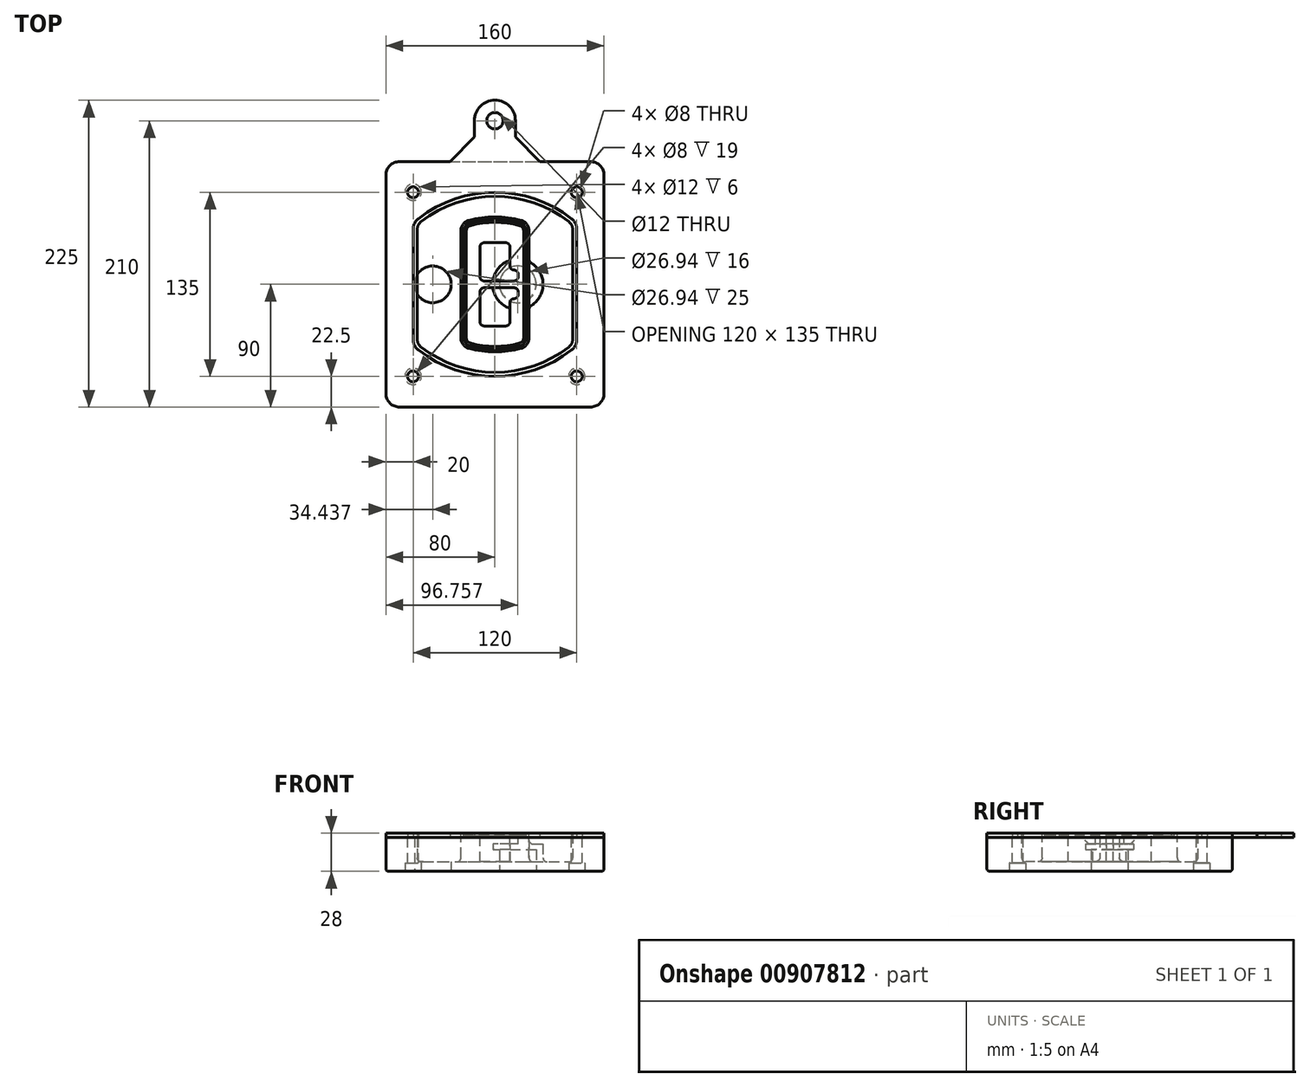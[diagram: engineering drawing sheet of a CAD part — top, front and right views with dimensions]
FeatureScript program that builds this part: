
annotation { "Feature Type Name" : "Feature", "Feature Type Description" : "" }
export const myFeature = defineFeature(function(context is Context, id is Id, definition is map)
    precondition{}
    {
        {
            var Q0;
            Q0=qCreatedBy(makeId("Top.planeOp"),FACE);
            var sketch = newSketch(context, id + "F0", { "sketchPlane" : qUnion([Q0])});
            skPoint(sketch, "E0.rect.middle", {"position": v(0, 0) * mm});
            skLineSegment(sketch, "E1.bottom", {"start": v(-70, -90) * mm, "end": v(70, -90) * mm});
            skLineSegment(sketch, "E1.top", {"start": v(-70, 90) * mm, "end": v(70, 90) * mm});
            skLineSegment(sketch, "E1.left", {"start": v(-80, -80) * mm, "end": v(-80, 80) * mm});
            skLineSegment(sketch, "E1.right", {"start": v(80, -80) * mm, "end": v(80, 80) * mm});
            skLineSegment(sketch, "E2", {"start": v(-80, 90) * mm, "end": v(80, -90) * mm, "construction": true});
            skLineSegment(sketch, "E3", {"start": v(80, 90) * mm, "end": v(-80, -90) * mm, "construction": true});
            skCircle(sketch, "E4", {"center": v(-60, 67.5) * mm, "radius": 4 * mm});
            skCircle(sketch, "E5", {"center": v(60, 67.5) * mm, "radius": 4 * mm});
            skCircle(sketch, "E6", {"center": v(60, -67.5) * mm, "radius": 4 * mm});
            skCircle(sketch, "E7", {"center": v(-60, -67.5) * mm, "radius": 4 * mm});
            skLineSegment(sketch, "E8", {"start": v(-60, 67.5) * mm, "end": v(60, 67.5) * mm, "construction": true});
            skLineSegment(sketch, "E9", {"start": v(60, 67.5) * mm, "end": v(60, -67.5) * mm, "construction": true});
            skLineSegment(sketch, "E10", {"start": v(60, -67.5) * mm, "end": v(-60, -67.5) * mm, "construction": true});
            skLineSegment(sketch, "E11", {"start": v(-60, -67.5) * mm, "end": v(-60, 67.5) * mm, "construction": true});
            skLineSegment(sketch, "E12", {"start": v(-60, 40.3) * mm, "end": v(-60, -40.3) * mm});
            skLineSegment(sketch, "E13", {"start": v(60, 40.3) * mm, "end": v(60, -40.3) * mm});
            skArc(sketch, "E14", {"start": v(56.15, 48.18) * mm, "mid": v(0, 67.5) * mm, "end": v(-56.15, 48.18) * mm});
            skArc(sketch, "E15", {"start": v(-56.15, -48.18) * mm, "mid": v(0, -67.5) * mm, "end": v(56.15, -48.18) * mm});
            skLineSegment(sketch, "E16", {"start": v(-60, 0) * mm, "end": v(60, 0) * mm, "construction": true});
            skPoint(sketch, "E17.visualSharp", {"position": v(-60, -45) * mm});
            skArc(sketch, "E17.filletArc", {"start": v(-60, -40.3) * mm, "mid": v(-58.99, -44.68) * mm, "end": v(-56.15, -48.18) * mm});
            skPoint(sketch, "E18.visualSharp", {"position": v(-60, 45) * mm});
            skArc(sketch, "E18.filletArc", {"start": v(-56.15, 48.18) * mm, "mid": v(-58.99, 44.68) * mm, "end": v(-60, 40.3) * mm});
            skPoint(sketch, "E19.visualSharp", {"position": v(60, 45) * mm});
            skArc(sketch, "E19.filletArc", {"start": v(60, 40.3) * mm, "mid": v(58.99, 44.68) * mm, "end": v(56.15, 48.18) * mm});
            skPoint(sketch, "E20.visualSharp", {"position": v(60, -45) * mm});
            skArc(sketch, "E20.filletArc", {"start": v(56.15, -48.18) * mm, "mid": v(58.99, -44.68) * mm, "end": v(60, -40.3) * mm});
            skPoint(sketch, "E21.visualSharp", {"position": v(-80, 90) * mm});
            skArc(sketch, "E21.filletArc", {"start": v(-70, 90) * mm, "mid": v(-77.07, 87.07) * mm, "end": v(-80, 80) * mm});
            skPoint(sketch, "E22.visualSharp", {"position": v(80, 90) * mm});
            skArc(sketch, "E22.filletArc", {"start": v(80, 80) * mm, "mid": v(77.07, 87.07) * mm, "end": v(70, 90) * mm});
            skPoint(sketch, "E23.visualSharp", {"position": v(80, -90) * mm});
            skArc(sketch, "E23.filletArc", {"start": v(70, -90) * mm, "mid": v(77.07, -87.07) * mm, "end": v(80, -80) * mm});
            skPoint(sketch, "E24.visualSharp", {"position": v(-80, -90) * mm});
            skArc(sketch, "E24.filletArc", {"start": v(-80, -80) * mm, "mid": v(-77.07, -87.07) * mm, "end": v(-70, -90) * mm});
            skArc(sketch, "E25.0", {"start": v(57, 40.3) * mm, "mid": v(56.3, 43.36) * mm, "end": v(54.3, 45.81) * mm});
            skLineSegment(sketch, "E25.1", {"start": v(57, 40.3) * mm, "end": v(57, -40.3) * mm});
            skArc(sketch, "E25.2", {"start": v(54.3, -45.81) * mm, "mid": v(56.3, -43.36) * mm, "end": v(57, -40.3) * mm});
            skArc(sketch, "E25.3", {"start": v(-54.3, -45.81) * mm, "mid": v(0, -64.5) * mm, "end": v(54.3, -45.81) * mm});
            skArc(sketch, "E25.4", {"start": v(-57, -40.3) * mm, "mid": v(-56.3, -43.36) * mm, "end": v(-54.3, -45.81) * mm});
            skArc(sketch, "E25.5", {"start": v(54.3, 45.81) * mm, "mid": v(0, 64.5) * mm, "end": v(-54.3, 45.81) * mm});
            skLineSegment(sketch, "E25.6", {"start": v(-57, 40.3) * mm, "end": v(-57, -40.3) * mm});
            skArc(sketch, "E25.7", {"start": v(-54.3, 45.81) * mm, "mid": v(-56.3, 43.36) * mm, "end": v(-57, 40.3) * mm});
            skArc(sketch, "E26.0", {"start": v(-58.62, 51.33) * mm, "mid": v(-62.58, 46.43) * mm, "end": v(-64, 40.3) * mm});
            skArc(sketch, "E26.1", {"start": v(58.62, 51.33) * mm, "mid": v(0, 71.5) * mm, "end": v(-58.62, 51.33) * mm});
            skArc(sketch, "E26.2", {"start": v(64, 40.3) * mm, "mid": v(62.58, 46.43) * mm, "end": v(58.62, 51.33) * mm});
            skLineSegment(sketch, "E26.3", {"start": v(64, 40.3) * mm, "end": v(64, -40.3) * mm});
            skArc(sketch, "E26.4", {"start": v(58.62, -51.33) * mm, "mid": v(62.58, -46.43) * mm, "end": v(64, -40.3) * mm});
            skLineSegment(sketch, "E26.5", {"start": v(-64, 40.3) * mm, "end": v(-64, -40.3) * mm});
            skArc(sketch, "E26.6", {"start": v(-58.62, -51.33) * mm, "mid": v(0, -71.5) * mm, "end": v(58.62, -51.33) * mm});
            skArc(sketch, "E26.7", {"start": v(-64, -40.3) * mm, "mid": v(-62.58, -46.43) * mm, "end": v(-58.62, -51.33) * mm});
            skSolve(sketch);
        }
        {
            var Q0;
            Q0=makeQuery(id+"F0.imprint","IMPRINT",FACE,{"disambiguationData":[TD([[makeQuery(id+"F0.imprint","IMPRINT",EDGE,{"derivedFrom":sQuery(id+"F0.wireOp",EDGE,"E1.bottom")}),1.0]])]});
            var Q1;
            Q1=makeQuery(id+"F0.imprint","IMPRINT",FACE,{"disambiguationData":[TD([[makeQuery(id+"F0.imprint","IMPRINT",EDGE,{"derivedFrom":sQuery(id+"F0.wireOp",EDGE,"E12")}),1.0]])]});
            var Q2;
            Q2=makeQuery(id+"F0.imprint","IMPRINT",FACE,{"disambiguationData":[TD([[makeQuery(id+"F0.imprint","IMPRINT",EDGE,{"derivedFrom":sQuery(id+"F0.wireOp",EDGE,"E25.0")}),1.0]])]});
            var Q3;
            Q3=makeQuery(id+"F0.imprint","IMPRINT",FACE,{"disambiguationData":[TD([[makeQuery(id+"F0.imprint","IMPRINT",EDGE,{"derivedFrom":sQuery(id+"F0.wireOp",EDGE,"E12")}),-1.0]])]});
            extrude(context, id + "F1", {"entities" : qUnion([Q0, Q1, Q2, Q3]), "oppositeDirection" : true, "depth" : 25 * mm});
        }
        {
            var Q0;
            Q0=makeQuery(id+"F0.imprint","IMPRINT",FACE,{"disambiguationData":[TD([[makeQuery(id+"F0.imprint","IMPRINT",EDGE,{"derivedFrom":sQuery(id+"F0.wireOp",EDGE,"E12")}),1.0]])]});
            extrude(context, id + "F2", {"entities" : qUnion([Q0]), "operationType" : NewBodyOperationType.ADD, "depth" : 3 * mm});
        }
        {
            var Q0;
            Q0=makeQuery(id+"F0.imprint","IMPRINT",FACE,{"disambiguationData":[TD([[makeQuery(id+"F0.imprint","IMPRINT",EDGE,{"derivedFrom":sQuery(id+"F0.wireOp",EDGE,"E25.0")}),1.0]])]});
            extrude(context, id + "F3", {"entities" : qUnion([Q0]), "operationType" : NewBodyOperationType.REMOVE, "oppositeDirection" : true, "depth" : 18 * mm});
        }
        {
            var Q0;
            Q0=makeQuery(id+"F2.opExtrude","CAP_FACE",FACE,{"disambiguationData":[OSD([sQuery(id+"F0.wireOp",EDGE,"E12"),sQuery(id+"F0.wireOp",EDGE,"E13"),sQuery(id+"F0.wireOp",EDGE,"E14"),sQuery(id+"F0.wireOp",EDGE,"E15"),sQuery(id+"F0.wireOp",EDGE,"E17.filletArc"),sQuery(id+"F0.wireOp",EDGE,"E18.filletArc"),sQuery(id+"F0.wireOp",EDGE,"E19.filletArc"),sQuery(id+"F0.wireOp",EDGE,"E20.filletArc"),sQuery(id+"F0.wireOp",EDGE,"E25.0"),sQuery(id+"F0.wireOp",EDGE,"E25.1"),sQuery(id+"F0.wireOp",EDGE,"E25.2"),sQuery(id+"F0.wireOp",EDGE,"E25.3"),sQuery(id+"F0.wireOp",EDGE,"E25.4"),sQuery(id+"F0.wireOp",EDGE,"E25.5"),sQuery(id+"F0.wireOp",EDGE,"E25.6"),sQuery(id+"F0.wireOp",EDGE,"E25.7")])],"isStart":false});
            var sketch = newSketch(context, id + "F4", { "sketchPlane" : qUnion([Q0])});
            skArc(sketch, "E27.0", {"start": v(-19.08, -46.97) * mm, "mid": v(0, -49.5) * mm, "end": v(19.08, -46.97) * mm});
            skArc(sketch, "E28.0", {"start": v(19.08, 46.97) * mm, "mid": v(0, 49.5) * mm, "end": v(-19.08, 46.97) * mm});
            skLineSegment(sketch, "E29", {"start": v(-25, 39.25) * mm, "end": v(-25, -39.25) * mm});
            skLineSegment(sketch, "E30", {"start": v(25, 39.25) * mm, "end": v(25, -39.25) * mm});
            skLineSegment(sketch, "E31", {"start": v(-25, 45.1) * mm, "end": v(25, 45.1) * mm, "construction": true});
            skLineSegment(sketch, "E32", {"start": v(-25, -45.1) * mm, "end": v(25, -45.1) * mm, "construction": true});
            skPoint(sketch, "E33.visualSharp", {"position": v(-25, 45.1) * mm});
            skArc(sketch, "E33.filletArc", {"start": v(-19.08, 46.97) * mm, "mid": v(-23.35, 44.11) * mm, "end": v(-25, 39.25) * mm});
            skPoint(sketch, "E34.visualSharp", {"position": v(25, 45.1) * mm});
            skArc(sketch, "E34.filletArc", {"start": v(25, 39.25) * mm, "mid": v(23.35, 44.11) * mm, "end": v(19.08, 46.97) * mm});
            skPoint(sketch, "E35.visualSharp", {"position": v(25, -45.1) * mm});
            skArc(sketch, "E35.filletArc", {"start": v(19.08, -46.97) * mm, "mid": v(23.35, -44.11) * mm, "end": v(25, -39.25) * mm});
            skPoint(sketch, "E36.visualSharp", {"position": v(-25, -45.1) * mm});
            skArc(sketch, "E36.filletArc", {"start": v(-25, -39.25) * mm, "mid": v(-23.35, -44.11) * mm, "end": v(-19.08, -46.97) * mm});
            skArc(sketch, "E37.0", {"start": v(54.3, 45.81) * mm, "mid": v(0, 64.5) * mm, "end": v(-54.3, 45.81) * mm});
            skArc(sketch, "E37.1", {"start": v(-54.3, 45.81) * mm, "mid": v(-56.3, 43.36) * mm, "end": v(-57, 40.3) * mm});
            skLineSegment(sketch, "E37.2", {"start": v(-57, 40.3) * mm, "end": v(-57, -40.3) * mm});
            skArc(sketch, "E37.3", {"start": v(-57, -40.3) * mm, "mid": v(-56.3, -43.36) * mm, "end": v(-54.3, -45.81) * mm});
            skArc(sketch, "E37.4", {"start": v(-54.3, -45.81) * mm, "mid": v(0, -64.5) * mm, "end": v(54.3, -45.81) * mm});
            skArc(sketch, "E37.5", {"start": v(54.3, -45.81) * mm, "mid": v(56.3, -43.36) * mm, "end": v(57, -40.3) * mm});
            skLineSegment(sketch, "E37.6", {"start": v(57, 40.3) * mm, "end": v(57, -40.3) * mm});
            skArc(sketch, "E37.7", {"start": v(57, 40.3) * mm, "mid": v(56.3, 43.36) * mm, "end": v(54.3, 45.81) * mm});
            skLineSegment(sketch, "E38.0", {"start": v(23, 39.25) * mm, "end": v(23, -39.25) * mm});
            skArc(sketch, "E38.1", {"start": v(18.56, -45.04) * mm, "mid": v(21.76, -42.9) * mm, "end": v(23, -39.25) * mm});
            skArc(sketch, "E38.2", {"start": v(-18.56, -45.04) * mm, "mid": v(0, -47.5) * mm, "end": v(18.56, -45.04) * mm});
            skArc(sketch, "E38.3", {"start": v(-23, -39.25) * mm, "mid": v(-21.76, -42.9) * mm, "end": v(-18.56, -45.04) * mm});
            skLineSegment(sketch, "E38.4", {"start": v(-23, 39.25) * mm, "end": v(-23, -39.25) * mm});
            skArc(sketch, "E38.5", {"start": v(23, 39.25) * mm, "mid": v(21.76, 42.9) * mm, "end": v(18.56, 45.04) * mm});
            skArc(sketch, "E38.6", {"start": v(-18.56, 45.04) * mm, "mid": v(-21.76, 42.9) * mm, "end": v(-23, 39.25) * mm});
            skArc(sketch, "E38.7", {"start": v(18.56, 45.04) * mm, "mid": v(0, 47.5) * mm, "end": v(-18.56, 45.04) * mm});
            skArc(sketch, "E39.0", {"start": v(21, 39.25) * mm, "mid": v(20.18, 41.68) * mm, "end": v(18.04, 43.1) * mm});
            skLineSegment(sketch, "E39.1", {"start": v(21, 39.25) * mm, "end": v(21, -39.25) * mm});
            skArc(sketch, "E39.2", {"start": v(18.04, -43.1) * mm, "mid": v(20.18, -41.68) * mm, "end": v(21, -39.25) * mm});
            skArc(sketch, "E39.3", {"start": v(-18.04, -43.1) * mm, "mid": v(0, -45.5) * mm, "end": v(18.04, -43.1) * mm});
            skArc(sketch, "E39.4", {"start": v(-21, -39.25) * mm, "mid": v(-20.18, -41.68) * mm, "end": v(-18.04, -43.1) * mm});
            skArc(sketch, "E39.5", {"start": v(18.04, 43.1) * mm, "mid": v(0, 45.5) * mm, "end": v(-18.04, 43.1) * mm});
            skLineSegment(sketch, "E39.6", {"start": v(-21, 39.25) * mm, "end": v(-21, -39.25) * mm});
            skArc(sketch, "E39.7", {"start": v(-18.04, 43.1) * mm, "mid": v(-20.18, 41.68) * mm, "end": v(-21, 39.25) * mm});
            skLineSegment(sketch, "E40", {"start": v(-25, 0) * mm, "end": v(25, 0) * mm, "construction": true});
            skLineSegment(sketch, "E41", {"start": v(-11, 5.5) * mm, "end": v(-11, 27.5) * mm});
            skLineSegment(sketch, "E42", {"start": v(-8, 30.5) * mm, "end": v(8, 30.5) * mm});
            skLineSegment(sketch, "E43", {"start": v(11, 27.5) * mm, "end": v(11, 13.5) * mm});
            skLineSegment(sketch, "E44", {"start": v(14, 10.5) * mm, "end": v(14, 10.5) * mm});
            skLineSegment(sketch, "E45", {"start": v(17, 7.5) * mm, "end": v(17, 5.5) * mm});
            skLineSegment(sketch, "E46", {"start": v(14, 2.5) * mm, "end": v(-8, 2.5) * mm});
            skPoint(sketch, "E47.visualSharp", {"position": v(-11, 30.5) * mm});
            skArc(sketch, "E47.filletArc", {"start": v(-8, 30.5) * mm, "mid": v(-10.12, 29.62) * mm, "end": v(-11, 27.5) * mm});
            skPoint(sketch, "E48.visualSharp", {"position": v(11, 30.5) * mm});
            skArc(sketch, "E48.filletArc", {"start": v(11, 27.5) * mm, "mid": v(10.12, 29.62) * mm, "end": v(8, 30.5) * mm});
            skPoint(sketch, "E49.visualSharp", {"position": v(11, 10.5) * mm});
            skArc(sketch, "E49.filletArc", {"start": v(11, 13.5) * mm, "mid": v(11.88, 11.38) * mm, "end": v(14, 10.5) * mm});
            skPoint(sketch, "E50.visualSharp", {"position": v(17, 10.5) * mm});
            skArc(sketch, "E50.filletArc", {"start": v(17, 7.5) * mm, "mid": v(16.12, 9.62) * mm, "end": v(14, 10.5) * mm});
            skPoint(sketch, "E51.visualSharp", {"position": v(17, 2.5) * mm});
            skArc(sketch, "E51.filletArc", {"start": v(14, 2.5) * mm, "mid": v(16.12, 3.38) * mm, "end": v(17, 5.5) * mm});
            skPoint(sketch, "E52.visualSharp", {"position": v(-11, 2.5) * mm});
            skArc(sketch, "E52.filletArc", {"start": v(-11, 5.5) * mm, "mid": v(-10.12, 3.38) * mm, "end": v(-8, 2.5) * mm});
            skLineSegment(sketch, "E53.0.MirrorCS", {"start": v(14, -2.5) * mm, "end": v(-8, -2.5) * mm});
            skArc(sketch, "E54.0.MirrorCS", {"start": v(-11, -5.5) * mm, "mid": v(-10.12, -3.38) * mm, "end": v(-8, -2.5) * mm});
            skLineSegment(sketch, "E55.0.MirrorCS", {"start": v(-11, -5.5) * mm, "end": v(-11, -27.5) * mm});
            skArc(sketch, "E56.0.MirrorCS", {"start": v(-8, -30.5) * mm, "mid": v(-10.12, -29.62) * mm, "end": v(-11, -27.5) * mm});
            skLineSegment(sketch, "E57.0.MirrorCS", {"start": v(-8, -30.5) * mm, "end": v(8, -30.5) * mm});
            skArc(sketch, "E58.0.MirrorCS", {"start": v(11, -27.5) * mm, "mid": v(10.12, -29.62) * mm, "end": v(8, -30.5) * mm});
            skLineSegment(sketch, "E59.0.MirrorCS", {"start": v(11, -27.5) * mm, "end": v(11, -13.5) * mm});
            skArc(sketch, "E60.0.MirrorCS", {"start": v(11, -13.5) * mm, "mid": v(11.88, -11.38) * mm, "end": v(14, -10.5) * mm});
            skArc(sketch, "E61.0.MirrorCS", {"start": v(17, -7.5) * mm, "mid": v(16.12, -9.62) * mm, "end": v(14, -10.5) * mm});
            skLineSegment(sketch, "E62.0.MirrorCS", {"start": v(17, -7.5) * mm, "end": v(17, -5.5) * mm});
            skArc(sketch, "E63.0.MirrorCS", {"start": v(14, -2.5) * mm, "mid": v(16.12, -3.38) * mm, "end": v(17, -5.5) * mm});
            skSolve(sketch);
        }
        {
            var Q0;
            Q0=makeQuery(id+"F4.imprint","IMPRINT",FACE,{"disambiguationData":[TD([[makeQuery(id+"F4.imprint","IMPRINT",EDGE,{"derivedFrom":sQuery(id+"F4.wireOp",EDGE,"E27.0")}),1.0]])]});
            var Q1;
            Q1=makeQuery(id+"F4.imprint","IMPRINT",FACE,{"disambiguationData":[TD([[makeQuery(id+"F4.imprint","IMPRINT",EDGE,{"derivedFrom":sQuery(id+"F4.wireOp",EDGE,"E38.0")}),-1.0]])]});
            var Q2;
            Q2=makeQuery(id+"F4.imprint","IMPRINT",FACE,{"disambiguationData":[TD([[makeQuery(id+"F4.imprint","IMPRINT",EDGE,{"derivedFrom":sQuery(id+"F4.wireOp",EDGE,"E39.0")}),1.0]])]});
            extrude(context, id + "F5", {"entities" : qUnion([Q0, Q1, Q2]), "operationType" : NewBodyOperationType.ADD, "endBound" : BoundingType.UP_TO_NEXT, "oppositeDirection" : true, "depth" : 25 * mm});
        }
        {
            var Q0;
            Q0=makeQuery(id+"F4.imprint","IMPRINT",FACE,{"disambiguationData":[TD([[makeQuery(id+"F4.imprint","IMPRINT",EDGE,{"derivedFrom":sQuery(id+"F4.wireOp",EDGE,"E38.0")}),-1.0]])]});
            extrude(context, id + "F6", {"entities" : qUnion([Q0]), "operationType" : NewBodyOperationType.REMOVE, "oppositeDirection" : true, "depth" : 2 * mm});
        }
        {
            var Q0;
            Q0=makeQuery(id+"F1.opExtrude","CAP_FACE",FACE,{"disambiguationData":[OSD([sQuery(id+"F0.wireOp",EDGE,"E1.bottom"),sQuery(id+"F0.wireOp",EDGE,"E1.top"),sQuery(id+"F0.wireOp",EDGE,"E1.left"),sQuery(id+"F0.wireOp",EDGE,"E1.right"),sQuery(id+"F0.wireOp",EDGE,"E4"),sQuery(id+"F0.wireOp",EDGE,"E5"),sQuery(id+"F0.wireOp",EDGE,"E6"),sQuery(id+"F0.wireOp",EDGE,"E7"),sQuery(id+"F0.wireOp",EDGE,"E21.filletArc"),sQuery(id+"F0.wireOp",EDGE,"E22.filletArc"),sQuery(id+"F0.wireOp",EDGE,"E23.filletArc"),sQuery(id+"F0.wireOp",EDGE,"E24.filletArc")])],"isStart":false});
            var sketch = newSketch(context, id + "F7", { "sketchPlane" : qUnion([Q0])});
            skCircle(sketch, "E64", {"center": v(16.76, 0) * mm, "radius": 13.47 * mm});
            skCircle(sketch, "E65", {"center": v(-45.56, 0) * mm, "radius": 13.47 * mm});
            skLineSegment(sketch, "E66", {"start": v(80, 0) * mm, "end": v(-80, 0) * mm});
            skCircle(sketch, "E67", {"center": v(16.76, 0) * mm, "radius": 18.47 * mm});
            skCircle(sketch, "E68", {"center": v(60, -67.5) * mm, "radius": 6 * mm});
            skCircle(sketch, "E69", {"center": v(-60, -67.5) * mm, "radius": 6 * mm});
            skCircle(sketch, "E70", {"center": v(-60, 67.5) * mm, "radius": 6 * mm});
            skCircle(sketch, "E71", {"center": v(60, 67.5) * mm, "radius": 6 * mm});
            skSolve(sketch);
        }
        {
            var Q0;
            {var subQ1=sQuery(id+"F7.wireOp",EDGE,"E66");var subQ4=sQuery(id+"F7.wireOp",EDGE,"E64");var subQ6=makeQuery(id+"F7.imprint","INTERSECT",VERTEX,{"disambiguationData":[OD(0.0)],"derivedFrom":[subQ4,subQ1]});Q0=makeQuery(id+"F7.imprint","IMPRINT",FACE,{"disambiguationData":[TD([[makeQuery(id+"F7.imprint","IMPRINT",EDGE,{"disambiguationData":[TD([[subQ6,-1.0]])],"derivedFrom":subQ4}),-1.0]])]});}
            var Q1;
            {var subQ0=sQuery(id+"F7.wireOp",EDGE,"E66");var subQ1=sQuery(id+"F7.wireOp",EDGE,"E64");var subQ3=makeQuery(id+"F7.imprint","INTERSECT",VERTEX,{"disambiguationData":[OD(0.0)],"derivedFrom":[subQ1,subQ0]});Q1=makeQuery(id+"F7.imprint","IMPRINT",FACE,{"disambiguationData":[TD([[makeQuery(id+"F7.imprint","IMPRINT",EDGE,{"disambiguationData":[TD([[subQ3,-1.0]])],"derivedFrom":subQ1}),1.0]])]});}
            var Q2;
            {var subQ0=sQuery(id+"F7.wireOp",EDGE,"E66");var subQ1=sQuery(id+"F7.wireOp",EDGE,"E64");var subQ3=makeQuery(id+"F7.imprint","INTERSECT",VERTEX,{"disambiguationData":[OD(0.0)],"derivedFrom":[subQ1,subQ0]});Q2=makeQuery(id+"F7.imprint","IMPRINT",FACE,{"disambiguationData":[TD([[makeQuery(id+"F7.imprint","IMPRINT",EDGE,{"disambiguationData":[TD([[subQ3,1.0]])],"derivedFrom":subQ1}),1.0]])]});}
            var Q3;
            {var subQ1=sQuery(id+"F7.wireOp",EDGE,"E66");var subQ4=sQuery(id+"F7.wireOp",EDGE,"E64");var subQ6=makeQuery(id+"F7.imprint","INTERSECT",VERTEX,{"disambiguationData":[OD(0.0)],"derivedFrom":[subQ4,subQ1]});Q3=makeQuery(id+"F7.imprint","IMPRINT",FACE,{"disambiguationData":[TD([[makeQuery(id+"F7.imprint","IMPRINT",EDGE,{"disambiguationData":[TD([[subQ6,1.0]])],"derivedFrom":subQ4}),-1.0]])]});}
            extrude(context, id + "F8", {"entities" : qUnion([Q0, Q1, Q2, Q3]), "operationType" : NewBodyOperationType.ADD, "oppositeDirection" : true, "depth" : 20 * mm});
        }
        {
            var Q0;
            {var subQ0=sQuery(id+"F7.wireOp",EDGE,"E66");var subQ1=sQuery(id+"F7.wireOp",EDGE,"E64");var subQ3=makeQuery(id+"F7.imprint","INTERSECT",VERTEX,{"disambiguationData":[OD(0.0)],"derivedFrom":[subQ1,subQ0]});Q0=makeQuery(id+"F7.imprint","IMPRINT",FACE,{"disambiguationData":[TD([[makeQuery(id+"F7.imprint","IMPRINT",EDGE,{"disambiguationData":[TD([[subQ3,-1.0]])],"derivedFrom":subQ1}),1.0]])]});}
            var Q1;
            {var subQ0=sQuery(id+"F7.wireOp",EDGE,"E66");var subQ1=sQuery(id+"F7.wireOp",EDGE,"E64");var subQ3=makeQuery(id+"F7.imprint","INTERSECT",VERTEX,{"disambiguationData":[OD(0.0)],"derivedFrom":[subQ1,subQ0]});Q1=makeQuery(id+"F7.imprint","IMPRINT",FACE,{"disambiguationData":[TD([[makeQuery(id+"F7.imprint","IMPRINT",EDGE,{"disambiguationData":[TD([[subQ3,1.0]])],"derivedFrom":subQ1}),1.0]])]});}
            extrude(context, id + "F9", {"entities" : qUnion([Q0, Q1]), "operationType" : NewBodyOperationType.REMOVE, "oppositeDirection" : true, "depth" : 16 * mm});
        }
        {
            var Q0;
            {var subQ0=sQuery(id+"F7.wireOp",EDGE,"E66");var subQ1=sQuery(id+"F7.wireOp",EDGE,"E65");var subQ3=makeQuery(id+"F7.imprint","INTERSECT",VERTEX,{"disambiguationData":[OD(0.0)],"derivedFrom":[subQ1,subQ0]});Q0=makeQuery(id+"F7.imprint","IMPRINT",FACE,{"disambiguationData":[TD([[makeQuery(id+"F7.imprint","IMPRINT",EDGE,{"disambiguationData":[TD([[subQ3,-1.0]])],"derivedFrom":subQ1}),1.0]])]});}
            var Q1;
            {var subQ0=sQuery(id+"F7.wireOp",EDGE,"E66");var subQ1=sQuery(id+"F7.wireOp",EDGE,"E65");var subQ3=makeQuery(id+"F7.imprint","INTERSECT",VERTEX,{"disambiguationData":[OD(0.0)],"derivedFrom":[subQ1,subQ0]});Q1=makeQuery(id+"F7.imprint","IMPRINT",FACE,{"disambiguationData":[TD([[makeQuery(id+"F7.imprint","IMPRINT",EDGE,{"disambiguationData":[TD([[subQ3,1.0]])],"derivedFrom":subQ1}),1.0]])]});}
            extrude(context, id + "F10", {"entities" : qUnion([Q0, Q1]), "operationType" : NewBodyOperationType.REMOVE, "oppositeDirection" : true, "depth" : 25 * mm});
        }
        {
            var Q0;
            Q0=makeQuery(id+"F7.imprint","IMPRINT",FACE,{"disambiguationData":[TD([[makeQuery(id+"F7.imprint","IMPRINT",EDGE,{"derivedFrom":sQuery(id+"F7.wireOp",EDGE,"E68")}),1.0]])]});
            var Q1;
            Q1=makeQuery(id+"F7.imprint","IMPRINT",FACE,{"disambiguationData":[TD([[makeQuery(id+"F7.imprint","IMPRINT",EDGE,{"derivedFrom":makeQuery(id+"F1.opExtrude","CAP_EDGE",EDGE,{"disambiguationData":[OSD([sQuery(id+"F0.wireOp",EDGE,"E5")])],"isStart":false})}),-1.0]])]});
            var Q2;
            Q2=makeQuery(id+"F7.imprint","IMPRINT",FACE,{"disambiguationData":[TD([[makeQuery(id+"F7.imprint","IMPRINT",EDGE,{"derivedFrom":sQuery(id+"F7.wireOp",EDGE,"E69")}),1.0]])]});
            var Q3;
            Q3=makeQuery(id+"F7.imprint","IMPRINT",FACE,{"disambiguationData":[TD([[makeQuery(id+"F7.imprint","IMPRINT",EDGE,{"derivedFrom":makeQuery(id+"F1.opExtrude","CAP_EDGE",EDGE,{"disambiguationData":[OSD([sQuery(id+"F0.wireOp",EDGE,"E4")])],"isStart":false})}),-1.0]])]});
            var Q4;
            Q4=makeQuery(id+"F7.imprint","IMPRINT",FACE,{"disambiguationData":[TD([[makeQuery(id+"F7.imprint","IMPRINT",EDGE,{"derivedFrom":sQuery(id+"F7.wireOp",EDGE,"E70")}),1.0]])]});
            var Q5;
            Q5=makeQuery(id+"F7.imprint","IMPRINT",FACE,{"disambiguationData":[TD([[makeQuery(id+"F7.imprint","IMPRINT",EDGE,{"derivedFrom":makeQuery(id+"F1.opExtrude","CAP_EDGE",EDGE,{"disambiguationData":[OSD([sQuery(id+"F0.wireOp",EDGE,"E7")])],"isStart":false})}),-1.0]])]});
            var Q6;
            Q6=makeQuery(id+"F7.imprint","IMPRINT",FACE,{"disambiguationData":[TD([[makeQuery(id+"F7.imprint","IMPRINT",EDGE,{"derivedFrom":sQuery(id+"F7.wireOp",EDGE,"E71")}),1.0]])]});
            var Q7;
            Q7=makeQuery(id+"F7.imprint","IMPRINT",FACE,{"disambiguationData":[TD([[makeQuery(id+"F7.imprint","IMPRINT",EDGE,{"derivedFrom":makeQuery(id+"F1.opExtrude","CAP_EDGE",EDGE,{"disambiguationData":[OSD([sQuery(id+"F0.wireOp",EDGE,"E6")])],"isStart":false})}),-1.0]])]});
            extrude(context, id + "F11", {"entities" : qUnion([Q0, Q1, Q2, Q3, Q4, Q5, Q6, Q7]), "operationType" : NewBodyOperationType.REMOVE, "oppositeDirection" : true, "depth" : 6 * mm});
        }
        {
            var Q0;
            Q0=makeQuery(id+"F9.boolean.opBoolean","COPY",FACE,{"derivedFrom":makeQuery(id+"F9.opExtrude","CAP_FACE",FACE,{"disambiguationData":[OSD([sQuery(id+"F7.wireOp",EDGE,"E64")])],"isStart":false})});
            var sketch = newSketch(context, id + "F12", { "sketchPlane" : qUnion([Q0])});
            skArc(sketch, "E72.0", {"start": v(11, 17.55) * mm, "mid": v(2.57, 11.82) * mm, "end": v(-1.54, 2.5) * mm});
            skArc(sketch, "E72.1", {"start": v(-1.54, -2.5) * mm, "mid": v(2.57, -11.82) * mm, "end": v(11, -17.55) * mm});
            skLineSegment(sketch, "E73", {"start": v(-1.54, -2.5) * mm, "end": v(14, -2.5) * mm});
            skLineSegment(sketch, "E74.0", {"start": v(14, 2.5) * mm, "end": v(-1.54, 2.5) * mm});
            skArc(sketch, "E74.1", {"start": v(14, 2.5) * mm, "mid": v(16.12, 3.38) * mm, "end": v(17, 5.5) * mm});
            skLineSegment(sketch, "E74.2", {"start": v(17, 7.5) * mm, "end": v(17, 5.5) * mm});
            skArc(sketch, "E74.3", {"start": v(17, 7.5) * mm, "mid": v(16.12, 9.62) * mm, "end": v(14, 10.5) * mm});
            skArc(sketch, "E74.4", {"start": v(11, 13.5) * mm, "mid": v(11.88, 11.38) * mm, "end": v(14, 10.5) * mm});
            skLineSegment(sketch, "E74.5", {"start": v(11, 17.55) * mm, "end": v(11, 13.5) * mm});
            skLineSegment(sketch, "E74.7", {"start": v(14, -2.5) * mm, "end": v(-1.54, -2.5) * mm});
            skArc(sketch, "E74.8", {"start": v(14, -2.5) * mm, "mid": v(16.12, -3.38) * mm, "end": v(17, -5.5) * mm});
            skLineSegment(sketch, "E74.9", {"start": v(17, -7.5) * mm, "end": v(17, -5.5) * mm});
            skArc(sketch, "E74.10", {"start": v(17, -7.5) * mm, "mid": v(16.12, -9.62) * mm, "end": v(14, -10.5) * mm});
            skArc(sketch, "E74.11", {"start": v(11, -13.5) * mm, "mid": v(11.88, -11.38) * mm, "end": v(14, -10.5) * mm});
            skLineSegment(sketch, "E74.12", {"start": v(11, -17.55) * mm, "end": v(11, -13.5) * mm});
            skPoint(sketch, "E75.orphan", {"position": v(11, -27.5) * mm});
            skPoint(sketch, "E76.orphan", {"position": v(-8, -2.5) * mm});
            skPoint(sketch, "E77.orphan", {"position": v(-8, 2.5) * mm});
            skPoint(sketch, "E78.orphan", {"position": v(11, 27.5) * mm});
            skSolve(sketch);
        }
        {
            var Q0;
            {var subQ7=sQuery(id+"F12.wireOp",EDGE,"E72.0");var subQ14=sQuery(id+"F12.wireOp",EDGE,"E72.1");var subQ16=sQuery(id+"F12.wireOp",EDGE,"E74.1");var subQ18=sQuery(id+"F12.wireOp",EDGE,"E74.8");Q0=qUnion([makeQuery(id+"F12.imprint","IMPRINT",FACE,{"disambiguationData":[TD([[makeQuery(id+"F12.imprint","IMPRINT",EDGE,{"derivedFrom":subQ7}),1.0]])]}),makeQuery(id+"F12.imprint","IMPRINT",FACE,{"disambiguationData":[TD([[makeQuery(id+"F12.imprint","IMPRINT",EDGE,{"derivedFrom":subQ14}),1.0]])]}),makeQuery(id+"F12.imprint","IMPRINT",FACE,{"disambiguationData":[TD([[makeQuery(id+"F12.imprint","IMPRINT",EDGE,{"derivedFrom":subQ16}),1.0]])]}),makeQuery(id+"F12.imprint","IMPRINT",FACE,{"disambiguationData":[TD([[makeQuery(id+"F12.imprint","IMPRINT",EDGE,{"derivedFrom":subQ18}),-1.0]])]})]);}
            var Q1;
            Q1=makeQuery(id+"F5.boolean.opBoolean","SPLIT",FACE,{"disambiguationData":[TD([makeQuery(id+"F5.opExtrude","SWEPT_FACE",FACE,{"disambiguationData":[OSD([sQuery(id+"F4.wireOp",EDGE,"E41")])]})])],"derivedFrom":makeQuery(id+"F3.boolean.opBoolean","COPY",FACE,{"derivedFrom":makeQuery(id+"F3.opExtrude","CAP_FACE",FACE,{"disambiguationData":[OSD([sQuery(id+"F0.wireOp",EDGE,"E25.0"),sQuery(id+"F0.wireOp",EDGE,"E25.1"),sQuery(id+"F0.wireOp",EDGE,"E25.2"),sQuery(id+"F0.wireOp",EDGE,"E25.3"),sQuery(id+"F0.wireOp",EDGE,"E25.4"),sQuery(id+"F0.wireOp",EDGE,"E25.5"),sQuery(id+"F0.wireOp",EDGE,"E25.6"),sQuery(id+"F0.wireOp",EDGE,"E25.7")])],"isStart":false})})});
            extrude(context, id + "F13", {"entities" : qUnion([Q0]), "operationType" : NewBodyOperationType.REMOVE, "endBound" : BoundingType.UP_TO_SURFACE, "endBoundEntityFace" : qUnion([Q1]), "depth" : 25 * mm});
        }
        {
            var Q0;
            Q0=makeQuery(id+"F3.boolean.opBoolean","COPY",EDGE,{"derivedFrom":makeQuery(id+"F3.opExtrude","CAP_EDGE",EDGE,{"disambiguationData":[OSD([sQuery(id+"F0.wireOp",EDGE,"E25.6")])],"isStart":false})});
            var Q1;
            Q1=makeQuery(id+"F8.boolean.opBoolean","INTERSECT",EDGE,{"derivedFrom":[makeQuery(id+"F5.opExtrude","SWEPT_FACE",FACE,{"disambiguationData":[OSD([sQuery(id+"F4.wireOp",EDGE,"E30")])]}),makeQuery(id+"F8.opExtrude","CAP_FACE",FACE,{"disambiguationData":[OSD([sQuery(id+"F7.wireOp",EDGE,"E67")])],"isStart":false})]});
            var Q2;
            Q2=makeQuery(id+"F8.boolean.opBoolean","INTERSECT",EDGE,{"disambiguationData":[OD(1.0)],"derivedFrom":[makeQuery(id+"F5.opExtrude","SWEPT_FACE",FACE,{"disambiguationData":[OSD([sQuery(id+"F4.wireOp",EDGE,"E30")])]}),makeQuery(id+"F8.opExtrude","SWEPT_FACE",FACE,{"disambiguationData":[OSD([sQuery(id+"F7.wireOp",EDGE,"E67")])]})]});
            var Q3;
            {var subQ0=sQuery(id+"F4.wireOp",EDGE,"E30");Q3=makeQuery(id+"F8.boolean.opBoolean","SPLIT",EDGE,{"disambiguationData":[TD([makeQuery(id+"F5.opExtrude","SWEPT_FACE",FACE,{"disambiguationData":[OSD([sQuery(id+"F4.wireOp",EDGE,"E35.filletArc")])]})])],"derivedFrom":makeQuery(id+"F5.opExtrude","CAP_EDGE",EDGE,{"disambiguationData":[OSD([subQ0])],"isStart":false})});}
            var Q4;
            {var subQ0=sQuery(id+"F0.wireOp",EDGE,"E25.7");var subQ1=sQuery(id+"F0.wireOp",EDGE,"E25.1");var subQ2=sQuery(id+"F0.wireOp",EDGE,"E25.6");var subQ3=sQuery(id+"F0.wireOp",EDGE,"E25.5");var subQ4=sQuery(id+"F0.wireOp",EDGE,"E25.4");var subQ5=sQuery(id+"F0.wireOp",EDGE,"E25.0");var subQ6=sQuery(id+"F0.wireOp",EDGE,"E25.2");var subQ7=sQuery(id+"F0.wireOp",EDGE,"E25.3");Q4=makeQuery(id+"F8.boolean.opBoolean","INTERSECT",EDGE,{"derivedFrom":[makeQuery(id+"F5.boolean.opBoolean","SPLIT",FACE,{"disambiguationData":[TD([makeQuery(id+"F2.opExtrude","SWEPT_FACE",FACE,{"disambiguationData":[OSD([subQ5])]})])],"derivedFrom":makeQuery(id+"F3.boolean.opBoolean","COPY",FACE,{"derivedFrom":makeQuery(id+"F3.opExtrude","CAP_FACE",FACE,{"disambiguationData":[OSD([subQ5,subQ1,subQ6,subQ7,subQ4,subQ3,subQ2,subQ0])],"isStart":false})})}),makeQuery(id+"F8.opExtrude","SWEPT_FACE",FACE,{"disambiguationData":[OSD([sQuery(id+"F7.wireOp",EDGE,"E67")])]})]});}
            var Q5;
            Q5=makeQuery(id+"F8.boolean.opBoolean","INTERSECT",EDGE,{"disambiguationData":[OD(0.0)],"derivedFrom":[makeQuery(id+"F5.opExtrude","SWEPT_FACE",FACE,{"disambiguationData":[OSD([sQuery(id+"F4.wireOp",EDGE,"E30")])]}),makeQuery(id+"F8.opExtrude","SWEPT_FACE",FACE,{"disambiguationData":[OSD([sQuery(id+"F7.wireOp",EDGE,"E67")])]})]});
            fillet(context, id + "F14", {"entities" : qUnion([Q0, Q1, Q2, Q3, Q4, Q5]), "radius" : 3 * mm, "tangentPropagation" : true, "allowEdgeOverflow" : false});
        }
        {
            var Q0;
            Q0=makeQuery(id+"F1.opExtrude","CAP_EDGE",EDGE,{"disambiguationData":[OSD([sQuery(id+"F0.wireOp",EDGE,"E1.bottom")])],"isStart":false});
            fillet(context, id + "F15", {"entities" : qUnion([Q0]), "radius" : 2 * mm, "tangentPropagation" : true, "allowEdgeOverflow" : false});
        }
        {
            var Q0;
            {var subQ0=sQuery(id+"F0.wireOp",EDGE,"E21.filletArc");var subQ1=sQuery(id+"F0.wireOp",EDGE,"E7");var subQ2=sQuery(id+"F0.wireOp",EDGE,"E6");var subQ3=sQuery(id+"F0.wireOp",EDGE,"E5");var subQ4=sQuery(id+"F0.wireOp",EDGE,"E4");var subQ5=sQuery(id+"F0.wireOp",EDGE,"E22.filletArc");var subQ6=sQuery(id+"F0.wireOp",EDGE,"E1.bottom");var subQ7=sQuery(id+"F0.wireOp",EDGE,"E1.right");var subQ8=sQuery(id+"F0.wireOp",EDGE,"E1.top");var subQ9=sQuery(id+"F0.wireOp",EDGE,"E1.left");var subQ10=sQuery(id+"F0.wireOp",EDGE,"E23.filletArc");var subQ11=sQuery(id+"F0.wireOp",EDGE,"E24.filletArc");Q0=makeQuery(id+"F2.boolean.opBoolean","SPLIT",FACE,{"disambiguationData":[TD([makeQuery(id+"F1.opExtrude","SWEPT_FACE",FACE,{"disambiguationData":[OSD([subQ6])]})])],"derivedFrom":makeQuery(id+"F1.opExtrude","CAP_FACE",FACE,{"disambiguationData":[OSD([subQ6,subQ8,subQ9,subQ7,subQ4,subQ3,subQ2,subQ1,subQ0,subQ5,subQ10,subQ11])],"isStart":true})});}
            var sketch = newSketch(context, id + "F16", { "sketchPlane" : qUnion([Q0])});
            skCircle(sketch, "E79", {"center": v(0, 120) * mm, "radius": 6 * mm});
            skLineSegment(sketch, "E80", {"start": v(0, 120) * mm, "end": v(0, 90) * mm, "construction": true});
            skArc(sketch, "E81", {"start": v(15, 120) * mm, "mid": v(0, 135) * mm, "end": v(-15, 120) * mm});
            skLineSegment(sketch, "E82", {"start": v(15, 120) * mm, "end": v(15, 108) * mm});
            skLineSegment(sketch, "E83", {"start": v(15, 108) * mm, "end": v(33, 90) * mm});
            skLineSegment(sketch, "E84", {"start": v(-15, 120) * mm, "end": v(-15, 108) * mm});
            skLineSegment(sketch, "E85", {"start": v(-15, 108) * mm, "end": v(-33, 90) * mm});
            skLineSegment(sketch, "E86", {"start": v(15, 120) * mm, "end": v(15, 120) * mm});
            skLineSegment(sketch, "E87", {"start": v(-80, 0) * mm, "end": v(80, 0) * mm, "construction": true});
            skLineSegment(sketch, "E88.MirrorCS", {"start": v(15, -120) * mm, "end": v(15, -120) * mm});
            skLineSegment(sketch, "E89.MirrorCS", {"start": v(0, -120) * mm, "end": v(0, -90) * mm, "construction": true});
            skArc(sketch, "E90.MirrorCS", {"start": v(15, -120) * mm, "mid": v(0, -135) * mm, "end": v(-15, -120) * mm});
            skLineSegment(sketch, "E91.MirrorCS", {"start": v(-15, -120) * mm, "end": v(-15, -108) * mm});
            skCircle(sketch, "E92.MirrorC", {"center": v(0, -120) * mm, "radius": 6 * mm});
            skLineSegment(sketch, "E93.MirrorCS", {"start": v(-15, -108) * mm, "end": v(-33, -90) * mm});
            skLineSegment(sketch, "E94.MirrorCS", {"start": v(15, -108) * mm, "end": v(33, -90) * mm});
            skLineSegment(sketch, "E95.MirrorCS", {"start": v(15, -120) * mm, "end": v(15, -108) * mm});
            skSolve(sketch);
        }
        {
            var Q0;
            Q0=makeQuery(id+"F16.imprint","IMPRINT",FACE,{"disambiguationData":[TD([[makeQuery(id+"F16.imprint","IMPRINT",EDGE,{"derivedFrom":sQuery(id+"F16.wireOp",EDGE,"E90.MirrorCS")}),-1.0]])]});
            var Q1;
            Q1=makeQuery(id+"F16.imprint","IMPRINT",FACE,{"disambiguationData":[TD([[makeQuery(id+"F16.imprint","IMPRINT",EDGE,{"derivedFrom":makeQuery(id+"F1.opExtrude","CAP_EDGE",EDGE,{"disambiguationData":[OSD([sQuery(id+"F0.wireOp",EDGE,"E1.left")])],"isStart":true})}),-1.0]])]});
            var Q2;
            Q2=makeQuery(id+"F16.imprint","IMPRINT",FACE,{"disambiguationData":[TD([[makeQuery(id+"F16.imprint","IMPRINT",EDGE,{"derivedFrom":sQuery(id+"F16.wireOp",EDGE,"E79")}),-1.0]])]});
            var Q3;
            Q3=makeQuery(id+"F2.opExtrude","CAP_FACE",FACE,{"disambiguationData":[OSD([sQuery(id+"F0.wireOp",EDGE,"E12"),sQuery(id+"F0.wireOp",EDGE,"E13"),sQuery(id+"F0.wireOp",EDGE,"E14"),sQuery(id+"F0.wireOp",EDGE,"E15"),sQuery(id+"F0.wireOp",EDGE,"E17.filletArc"),sQuery(id+"F0.wireOp",EDGE,"E18.filletArc"),sQuery(id+"F0.wireOp",EDGE,"E19.filletArc"),sQuery(id+"F0.wireOp",EDGE,"E20.filletArc"),sQuery(id+"F0.wireOp",EDGE,"E25.0"),sQuery(id+"F0.wireOp",EDGE,"E25.1"),sQuery(id+"F0.wireOp",EDGE,"E25.2"),sQuery(id+"F0.wireOp",EDGE,"E25.3"),sQuery(id+"F0.wireOp",EDGE,"E25.4"),sQuery(id+"F0.wireOp",EDGE,"E25.5"),sQuery(id+"F0.wireOp",EDGE,"E25.6"),sQuery(id+"F0.wireOp",EDGE,"E25.7")])],"isStart":false});
            extrude(context, id + "F17", {"entities" : qUnion([Q0, Q1, Q2]), "endBound" : BoundingType.UP_TO_SURFACE, "depth" : 25 * mm, "endBoundEntityFace" : qUnion([Q3]), "offsetDistance" : 25 * mm});
        }
    });
